# Revit family: Proto Table L53 H45
name_source: partatom
category: Furniture
revit_build: Autodesk Revit 2017 (Build: 20171027_0315(x64)
units: mm (PartAtom-declared; Revit-internal decimal feet)

## family parameters
Always vertical = Yes
Cut with Voids When Loaded = No
OmniClass Number = 23.40.20.00
OmniClass Title = General Furniture and Specialties
Room Calculation Point = No
Shared = No
Work Plane-Based = No

## types (1)
- Proto Table L53 H45
    Design Year = 2020
    Environment = FSC
    Gliders = +Halle Felt
    Height (cm) = 45
    Height (in) = 17,7
    Length (cm) = 53
    Length (in) = 20,9
    Packaging Dimensions (cm) = 54,5 / 43,5 / 46,5
    Packaging Dimensions (in) = 21,5 / 17,2 / 18,4
    Product family = Proto
    Table base = +Halle Oak Veneer Vertical
    Table top = +Halle Oak Solid Horizontal
    URL = https://www.plushalle.com
    Variations = Soap treated / Lacquered
    Warranty period = 2 years standard warranty
    Weight (kg) = 21,5
    Weight (lbs) = 47,7
    Width (cm) = 42
    Width (in) = 16,5

## geometry (parser evidence)
native form markers: Sweep x2
no freeform markers — native parametric forms only
